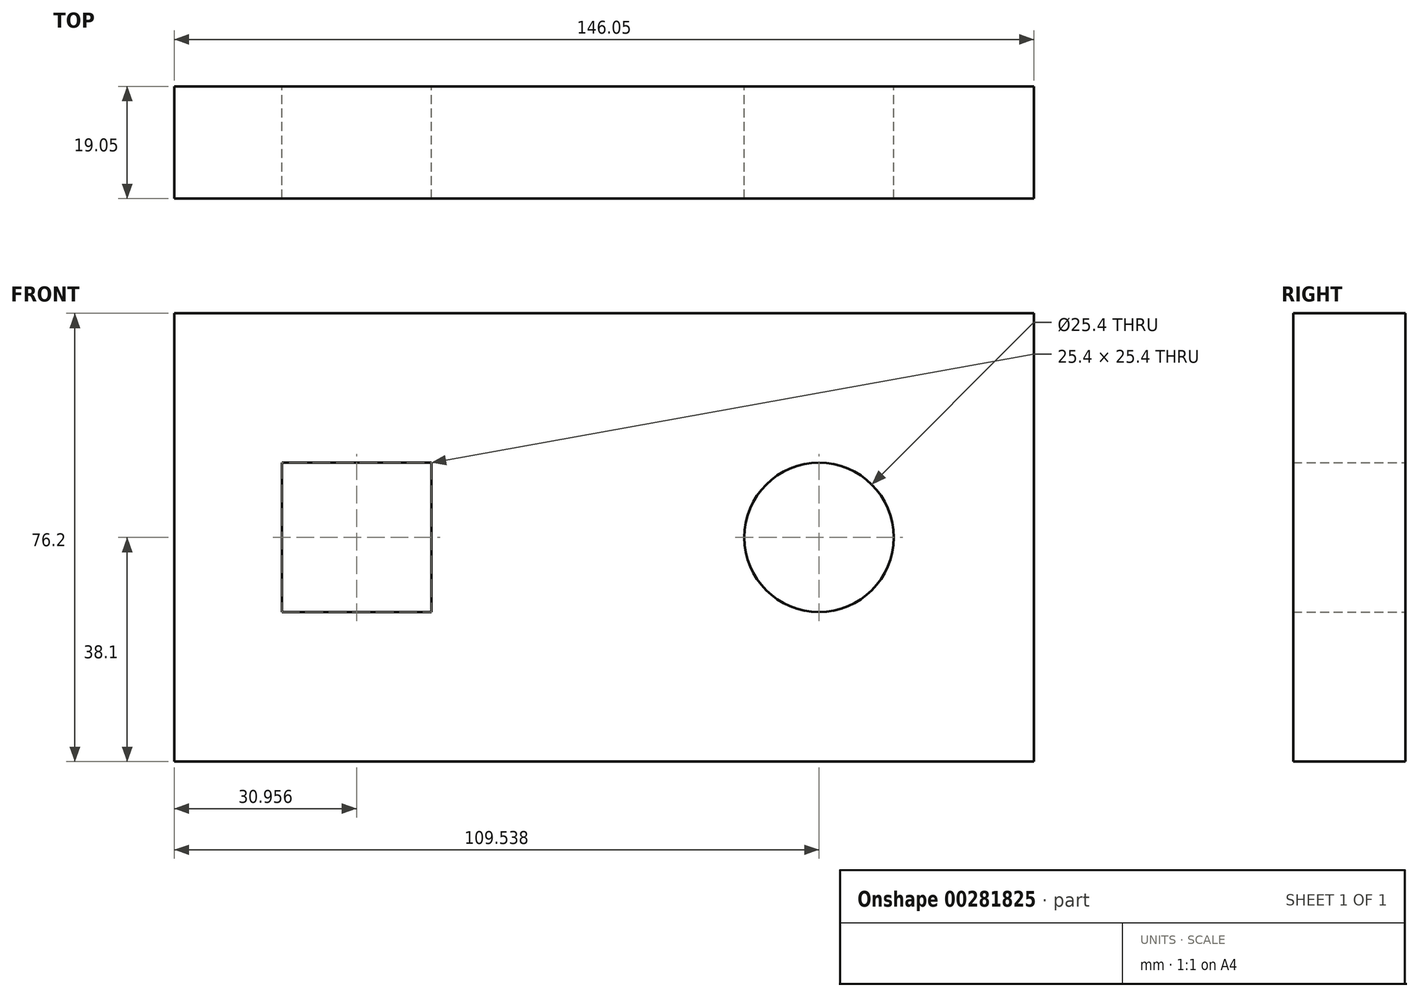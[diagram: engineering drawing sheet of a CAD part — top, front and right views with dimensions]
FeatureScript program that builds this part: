
annotation { "Feature Type Name" : "Feature", "Feature Type Description" : "" }
export const myFeature = defineFeature(function(context is Context, id is Id, definition is map)
    precondition{}
    {
        {
            var Q0;
            Q0=qCreatedBy(makeId("Front.planeOp"),FACE);
            var sketch = newSketch(context, id + "F0", { "sketchPlane" : qUnion([Q0])});
            skLineSegment(sketch, "E0.bottom", {"start": v(0, 0) * mm, "end": v(-146.05, 0) * mm});
            skLineSegment(sketch, "E0.top", {"start": v(0, 76.2) * mm, "end": v(-146.05, 76.2) * mm});
            skLineSegment(sketch, "E0.left", {"start": v(0, 0) * mm, "end": v(0, 76.2) * mm});
            skLineSegment(sketch, "E0.right", {"start": v(-146.05, 0) * mm, "end": v(-146.05, 76.2) * mm});
            skCircle(sketch, "E1", {"center": v(-36.51, 38.1) * mm, "radius": 12.7 * mm});
            skLineSegment(sketch, "E2.bottom", {"start": v(-127.8, 50.8) * mm, "end": v(-102.4, 50.8) * mm});
            skLineSegment(sketch, "E2.top", {"start": v(-127.8, 25.4) * mm, "end": v(-102.4, 25.4) * mm});
            skLineSegment(sketch, "E2.left", {"start": v(-127.8, 50.8) * mm, "end": v(-127.8, 25.4) * mm});
            skLineSegment(sketch, "E2.right", {"start": v(-102.4, 50.8) * mm, "end": v(-102.4, 25.4) * mm});
            skSolve(sketch);
        }
        {
            var Q0;
            Q0=makeQuery(id+"F0.imprint","IMPRINT",FACE,{"disambiguationData":[TD([[makeQuery(id+"F0.imprint","IMPRINT",EDGE,{"derivedFrom":sQuery(id+"F0.wireOp",EDGE,"E0.bottom")}),-1.0]])]});
            extrude(context, id + "F1", {"entities" : qUnion([Q0]), "depth" : 19.05 * mm});
        }
    });
